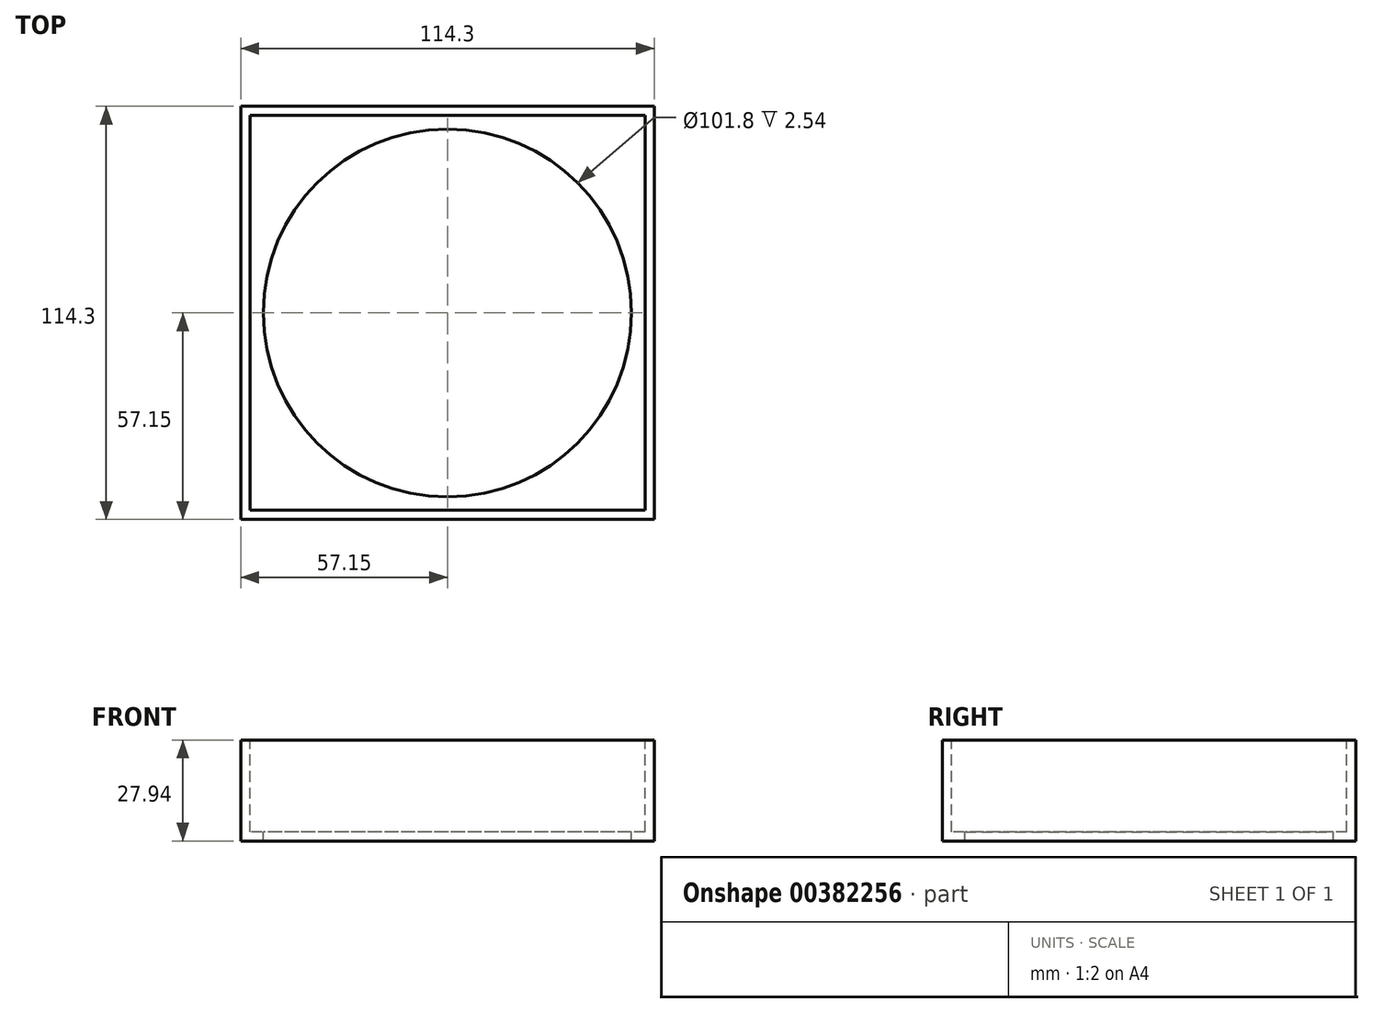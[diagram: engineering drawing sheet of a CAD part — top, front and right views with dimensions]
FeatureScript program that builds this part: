
annotation { "Feature Type Name" : "Feature", "Feature Type Description" : "" }
export const myFeature = defineFeature(function(context is Context, id is Id, definition is map)
    precondition{}
    {
        {
            var Q0;
            Q0=qCreatedBy(makeId("Top.planeOp"),FACE);
            var sketch = newSketch(context, id + "F0", { "sketchPlane" : qUnion([Q0])});
            skLineSegment(sketch, "E0.bottom", {"start": v(57.15, 57.15) * mm, "end": v(-57.15, 57.15) * mm});
            skLineSegment(sketch, "E0.top", {"start": v(57.15, -57.15) * mm, "end": v(-57.15, -57.15) * mm});
            skLineSegment(sketch, "E0.left", {"start": v(57.15, 57.15) * mm, "end": v(57.15, -57.15) * mm});
            skLineSegment(sketch, "E0.right", {"start": v(-57.15, 57.15) * mm, "end": v(-57.15, -57.15) * mm});
            skPoint(sketch, "E0.middle", {"position": v(0, 0) * mm});
            skSolve(sketch);
        }
        {
            var Q0;
            Q0=makeQuery(id+"F0.imprint","IMPRINT",FACE,{"disambiguationData":[TD([[makeQuery(id+"F0.imprint","IMPRINT",EDGE,{"derivedFrom":sQuery(id+"F0.wireOp",EDGE,"E0.bottom")}),1.0]])]});
            extrude(context, id + "F1", {"entities" : qUnion([Q0]), "depth" : 2.54 * mm});
        }
        {
            var Q0;
            Q0=makeQuery(id+"F1.opExtrude","SWEPT_FACE",FACE,{"disambiguationData":[OSD([sQuery(id+"F0.wireOp",EDGE,"E0.left")])]});
            var sketch = newSketch(context, id + "F2", { "sketchPlane" : qUnion([Q0])});
            skLineSegment(sketch, "E1.bottom", {"start": v(-57.15, 0) * mm, "end": v(57.15, 0) * mm});
            skLineSegment(sketch, "E2.top", {"start": v(-57.15, 27.94) * mm, "end": v(57.15, 27.94) * mm});
            skLineSegment(sketch, "E2.left", {"start": v(-57.15, 2.54) * mm, "end": v(-57.15, 27.94) * mm});
            skLineSegment(sketch, "E2.right", {"start": v(57.15, 2.54) * mm, "end": v(57.15, 27.94) * mm});
            skSolve(sketch);
        }
        {
            var Q0;
            Q0=makeQuery(id+"F2.imprint","IMPRINT",FACE,{"disambiguationData":[TD([[makeQuery(id+"F2.imprint","IMPRINT",EDGE,{"derivedFrom":sQuery(id+"F2.wireOp",EDGE,"E2.top")}),-1.0]])]});
            extrude(context, id + "F3", {"entities" : qUnion([Q0]), "oppositeDirection" : true, "depth" : 2.54 * mm});
        }
        {
            var Q0;
            Q0=makeQuery(id+"F3.opExtrude","SWEPT_BODY",BODY,{"disambiguationData":[OSD([sQuery(id+"F0.wireOp",EDGE,"E0.left"),sQuery(id+"F2.wireOp",EDGE,"E2.top"),sQuery(id+"F2.wireOp",EDGE,"E2.left"),sQuery(id+"F2.wireOp",EDGE,"E2.right")])]});
            var Q1;
            Q1=qCreatedBy(makeId("Right.planeOp"),FACE);
            mirror(context, id + "F4", {"operationType" : NewBodyOperationType.ADD, "entities" : qUnion([Q0]), "mirrorPlane" : qUnion([Q1])});
        }
        {
            var Q0;
            {var subQ0=makeQuery(id+"F3.opExtrude","SWEPT_FACE",FACE,{"disambiguationData":[OSD([sQuery(id+"F2.wireOp",EDGE,"E2.right")])]});Q0=makeQuery(id+"F4.boolean.opBoolean","MERGE",FACE,{"derivedFrom":[makeQuery(id+"F1.opExtrude","SWEPT_FACE",FACE,{"disambiguationData":[OSD([sQuery(id+"F0.wireOp",EDGE,"E0.bottom")])]}),subQ0,makeQuery(id+"F4.opPattern","COPY",FACE,{"derivedFrom":subQ0,"instanceName":"1"})]});}
            var sketch = newSketch(context, id + "F5", { "sketchPlane" : qUnion([Q0])});
            skLineSegment(sketch, "E3.bottom", {"start": v(-54.61, 2.54) * mm, "end": v(54.61, 2.54) * mm});
            skLineSegment(sketch, "E3.top", {"start": v(-54.61, 27.94) * mm, "end": v(54.61, 27.94) * mm});
            skLineSegment(sketch, "E3.left", {"start": v(-54.61, 2.54) * mm, "end": v(-54.61, 27.94) * mm});
            skLineSegment(sketch, "E3.right", {"start": v(54.61, 2.54) * mm, "end": v(54.61, 27.94) * mm});
            skSolve(sketch);
        }
        {
            var Q0;
            Q0=makeQuery(id+"F5.imprint","IMPRINT",FACE,{"disambiguationData":[TD([[makeQuery(id+"F5.imprint","IMPRINT",EDGE,{"derivedFrom":sQuery(id+"F5.wireOp",EDGE,"E3.bottom")}),1.0]])]});
            extrude(context, id + "F6", {"entities" : qUnion([Q0]), "oppositeDirection" : true, "depth" : 2.54 * mm});
        }
        {
            var Q0;
            Q0=makeQuery(id+"F6.opExtrude","SWEPT_BODY",BODY,{"disambiguationData":[OSD([sQuery(id+"F5.wireOp",EDGE,"E3.bottom"),sQuery(id+"F5.wireOp",EDGE,"E3.top"),sQuery(id+"F5.wireOp",EDGE,"E3.left"),sQuery(id+"F5.wireOp",EDGE,"E3.right")])]});
            var Q1;
            Q1=qCreatedBy(makeId("Front.planeOp"),FACE);
            mirror(context, id + "F7", {"operationType" : NewBodyOperationType.ADD, "entities" : qUnion([Q0]), "mirrorPlane" : qUnion([Q1])});
        }
        {
            var Q0;
            {var subQ0=makeQuery(id+"F6.opExtrude","SWEPT_FACE",FACE,{"disambiguationData":[OSD([sQuery(id+"F5.wireOp",EDGE,"E3.top")])]});var subQ1=makeQuery(id+"F3.opExtrude","SWEPT_FACE",FACE,{"disambiguationData":[OSD([sQuery(id+"F2.wireOp",EDGE,"E2.top")])]});Q0=makeQuery(id+"F7.boolean.opBoolean","MERGE",FACE,{"derivedFrom":[subQ1,makeQuery(id+"F4.opPattern","COPY",FACE,{"derivedFrom":subQ1,"instanceName":"1"}),subQ0,makeQuery(id+"F7.opPattern","COPY",FACE,{"derivedFrom":subQ0,"instanceName":"1"})]});}
            var sketch = newSketch(context, id + "F8", { "sketchPlane" : qUnion([Q0])});
            skLineSegment(sketch, "E4.bottom", {"start": v(57.15, 57.15) * mm, "end": v(-57.15, 57.15) * mm});
            skLineSegment(sketch, "E4.top", {"start": v(57.15, -57.15) * mm, "end": v(-57.15, -57.15) * mm});
            skLineSegment(sketch, "E4.left", {"start": v(57.15, 57.15) * mm, "end": v(57.15, -57.15) * mm});
            skLineSegment(sketch, "E4.right", {"start": v(-57.15, 57.15) * mm, "end": v(-57.15, -57.15) * mm});
            skSolve(sketch);
        }
        {
            var Q0;
            Q0=makeQuery(id+"F8.imprint","IMPRINT",FACE,{"disambiguationData":[TD([[makeQuery(id+"F8.imprint","IMPRINT",EDGE,{"derivedFrom":sQuery(id+"F8.wireOp",EDGE,"E4.bottom")}),-1.0]])]});
            var Q1;
            {var subQ0=makeQuery(id+"F6.opExtrude","CAP_EDGE",EDGE,{"disambiguationData":[OSD([sQuery(id+"F5.wireOp",EDGE,"E3.top")])],"isStart":false});Q1=makeQuery(id+"F8.imprint","IMPRINT",FACE,{"disambiguationData":[TD([[makeQuery(id+"F8.imprint","IMPRINT",EDGE,{"derivedFrom":subQ0}),1.0]])]});}
            extrude(context, id + "F9", {"entities" : qUnion([Q0, Q1]), "depth" : 2.54 * mm});
        }
        {
            var Q0;
            Q0=makeQuery(id+"F9.opExtrude","CAP_FACE",FACE,{"disambiguationData":[OSD([sQuery(id+"F8.wireOp",EDGE,"E4.bottom"),sQuery(id+"F8.wireOp",EDGE,"E4.top"),sQuery(id+"F8.wireOp",EDGE,"E4.left"),sQuery(id+"F8.wireOp",EDGE,"E4.right")])],"isStart":false});
            var sketch = newSketch(context, id + "F10", { "sketchPlane" : qUnion([Q0])});
            skLineSegment(sketch, "E5.bottom", {"start": v(57.15, 57.15) * mm, "end": v(-57.15, 57.15) * mm});
            skLineSegment(sketch, "E5.top", {"start": v(57.15, -57.15) * mm, "end": v(-57.15, -57.15) * mm});
            skLineSegment(sketch, "E5.left", {"start": v(57.15, 57.15) * mm, "end": v(57.15, -57.15) * mm});
            skLineSegment(sketch, "E5.right", {"start": v(-57.15, 57.15) * mm, "end": v(-57.15, -57.15) * mm});
            skSolve(sketch);
        }
        {
            var Q0;
            Q0=makeQuery(id+"F10.imprint","IMPRINT",FACE,{"disambiguationData":[TD([[makeQuery(id+"F10.imprint","IMPRINT",EDGE,{"derivedFrom":sQuery(id+"F10.wireOp",EDGE,"E5.bottom")}),-1.0]])]});
            extrude(context, id + "F11", {"entities" : qUnion([Q0]), "operationType" : NewBodyOperationType.ADD, "depth" : 2.54 * mm});
        }
        {
            var Q0;
            Q0=makeQuery(id+"F11.opExtrude","CAP_FACE",FACE,{"disambiguationData":[OSD([sQuery(id+"F10.wireOp",EDGE,"E5.bottom"),sQuery(id+"F10.wireOp",EDGE,"E5.top"),sQuery(id+"F10.wireOp",EDGE,"E5.left"),sQuery(id+"F10.wireOp",EDGE,"E5.right")])],"isStart":false});
            var sketch = newSketch(context, id + "F12", { "sketchPlane" : qUnion([Q0])});
            skLineSegment(sketch, "E6.bottom", {"start": v(-57.15, 57.15) * mm, "end": v(-52.07, 57.15) * mm});
            skLineSegment(sketch, "E6.top", {"start": v(-57.15, 52.07) * mm, "end": v(-52.07, 52.07) * mm});
            skLineSegment(sketch, "E6.left", {"start": v(-57.15, 57.15) * mm, "end": v(-57.15, 52.07) * mm});
            skLineSegment(sketch, "E6.right", {"start": v(-52.07, 57.15) * mm, "end": v(-52.07, 52.07) * mm});
            skLineSegment(sketch, "E7.bottom", {"start": v(-52.07, 52.07) * mm, "end": v(24.13, 52.07) * mm});
            skLineSegment(sketch, "E7.top", {"start": v(-52.07, -52.07) * mm, "end": v(24.13, -52.07) * mm});
            skLineSegment(sketch, "E7.left", {"start": v(-52.07, 52.07) * mm, "end": v(-52.07, -52.07) * mm});
            skLineSegment(sketch, "E7.right", {"start": v(24.13, 52.07) * mm, "end": v(24.13, -52.07) * mm});
            skSolve(sketch);
        }
        {
            var Q0;
            Q0=makeQuery(id+"F12.imprint","IMPRINT",FACE,{"disambiguationData":[TD([[makeQuery(id+"F12.imprint","IMPRINT",EDGE,{"derivedFrom":sQuery(id+"F12.wireOp",EDGE,"E7.bottom")}),-1.0]])]});
            extrude(context, id + "F13", {"entities" : qUnion([Q0]), "operationType" : NewBodyOperationType.REMOVE, "oppositeDirection" : true, "depth" : 1.27 * mm});
        }
        {
            var Q0;
            Q0=makeQuery(id+"F11.opExtrude","CAP_FACE",FACE,{"disambiguationData":[OSD([sQuery(id+"F10.wireOp",EDGE,"E5.bottom"),sQuery(id+"F10.wireOp",EDGE,"E5.top"),sQuery(id+"F10.wireOp",EDGE,"E5.left"),sQuery(id+"F10.wireOp",EDGE,"E5.right")])],"isStart":false});
            var sketch = newSketch(context, id + "F14", { "sketchPlane" : qUnion([Q0])});
            skLineSegment(sketch, "E8", {"start": v(0, 0) * mm, "end": v(40.64, 0) * mm, "construction": true});
            skPoint(sketch, "E8.endSnap0", {"position": v(24.13, 0) * mm});
            skCircle(sketch, "E9", {"center": v(40.64, 0) * mm, "radius": 6.35 * mm});
            skLineSegment(sketch, "E10", {"start": v(40.64, 0) * mm, "end": v(40.64, 45.72) * mm});
            skLineSegment(sketch, "E11", {"start": v(40.64, 45.72) * mm, "end": v(48.9, 45.72) * mm});
            skCircle(sketch, "E12", {"center": v(48.9, 45.72) * mm, "radius": 6.35 * mm});
            skCircle(sketch, "E13.MirrorC", {"center": v(32.39, 45.72) * mm, "radius": 6.35 * mm});
            skSolve(sketch);
        }
        {
            var Q0;
            Q0=makeQuery(id+"F14.imprint","IMPRINT",FACE,{"disambiguationData":[TD([[makeQuery(id+"F14.imprint","IMPRINT",EDGE,{"derivedFrom":sQuery(id+"F14.wireOp",EDGE,"E12")}),1.0]])]});
            var Q1;
            Q1=makeQuery(id+"F14.imprint","IMPRINT",FACE,{"disambiguationData":[TD([[makeQuery(id+"F14.imprint","IMPRINT",EDGE,{"derivedFrom":sQuery(id+"F14.wireOp",EDGE,"E13.MirrorC")}),-1.0]])]});
            var Q2;
            Q2=makeQuery(id+"F14.imprint","IMPRINT",FACE,{"disambiguationData":[TD([[makeQuery(id+"F14.imprint","IMPRINT",EDGE,{"derivedFrom":sQuery(id+"F14.wireOp",EDGE,"E9")}),1.0]])]});
            extrude(context, id + "F15", {"entities" : qUnion([Q0, Q1, Q2]), "operationType" : NewBodyOperationType.REMOVE, "oppositeDirection" : true, "depth" : 1.27 * mm});
        }
        {
            var Q0;
            Q0=makeQuery(id+"F9.opExtrude","SWEPT_BODY",BODY,{"disambiguationData":[OSD([sQuery(id+"F8.wireOp",EDGE,"E4.bottom"),sQuery(id+"F8.wireOp",EDGE,"E4.top"),sQuery(id+"F8.wireOp",EDGE,"E4.left"),sQuery(id+"F8.wireOp",EDGE,"E4.right")])]});
            deleteBodies(context, id + "F16", {"entities" : qUnion([Q0])});
        }
        {
            var Q0;
            Q0=makeQuery(id+"F1.opExtrude","CAP_FACE",FACE,{"disambiguationData":[OSD([sQuery(id+"F0.wireOp",EDGE,"E0.bottom"),sQuery(id+"F0.wireOp",EDGE,"E0.top"),sQuery(id+"F0.wireOp",EDGE,"E0.left"),sQuery(id+"F0.wireOp",EDGE,"E0.right")])],"isStart":false});
            var sketch = newSketch(context, id + "F17", { "sketchPlane" : qUnion([Q0])});
            skCircle(sketch, "E14", {"center": v(0, 0) * mm, "radius": 50.9 * mm});
            skSolve(sketch);
        }
        {
            var Q0;
            Q0=makeQuery(id+"F17.imprint","IMPRINT",FACE,{"disambiguationData":[TD([[makeQuery(id+"F17.imprint","IMPRINT",EDGE,{"derivedFrom":sQuery(id+"F17.wireOp",EDGE,"E14")}),1.0]])]});
            extrude(context, id + "F18", {"entities" : qUnion([Q0]), "operationType" : NewBodyOperationType.REMOVE, "endBound" : BoundingType.UP_TO_NEXT, "oppositeDirection" : true, "depth" : 25 * mm});
        }
    });
